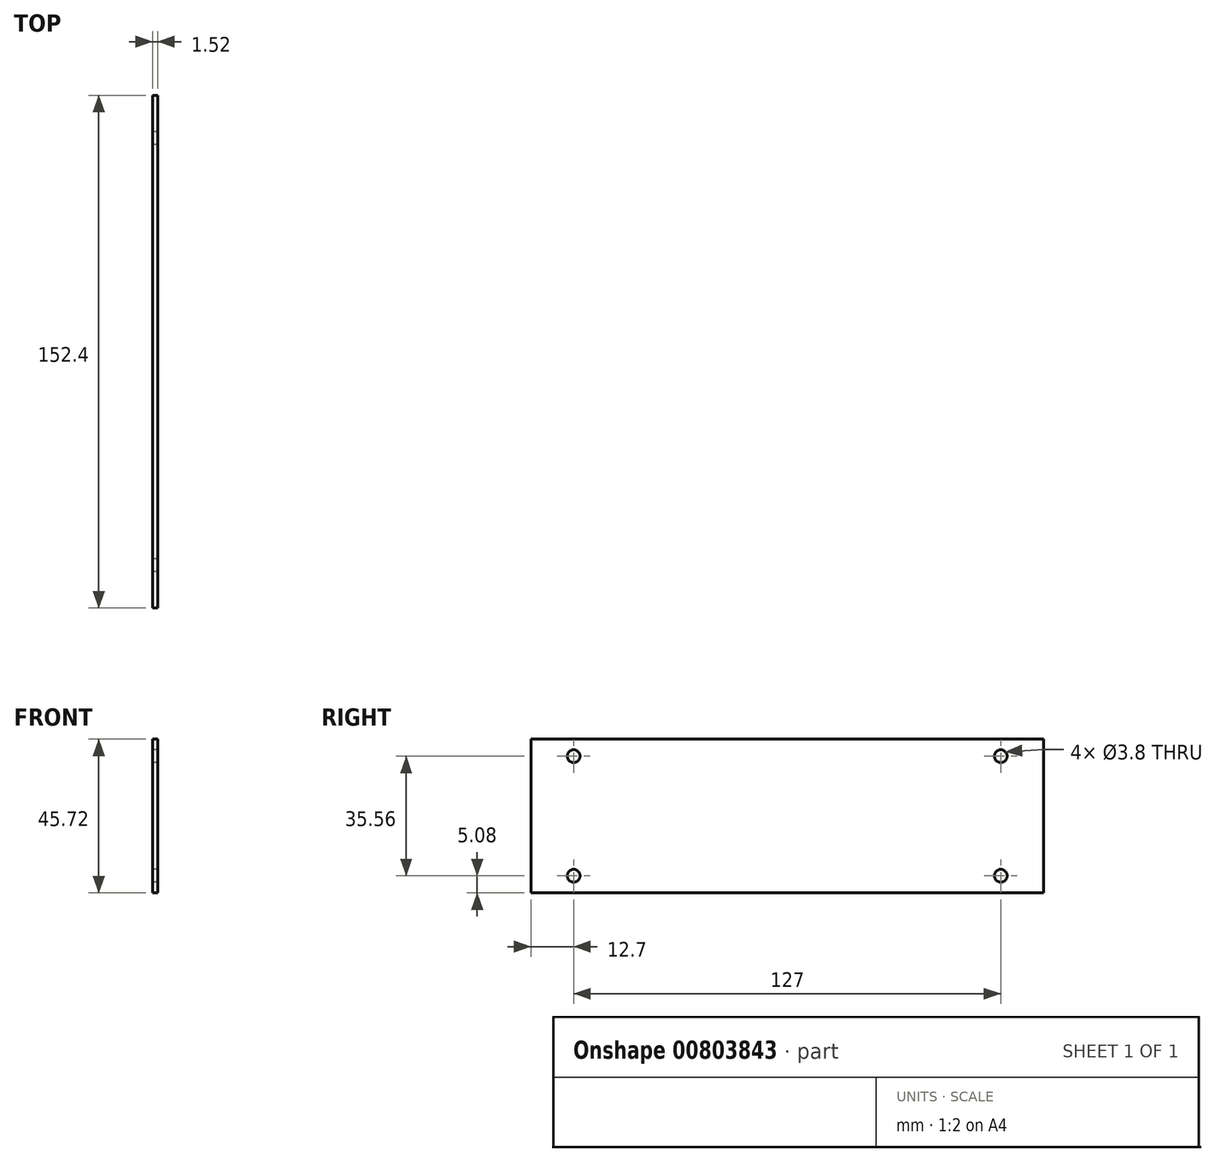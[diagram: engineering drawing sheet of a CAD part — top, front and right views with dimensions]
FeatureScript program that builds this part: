
annotation { "Feature Type Name" : "Feature", "Feature Type Description" : "" }
export const myFeature = defineFeature(function(context is Context, id is Id, definition is map)
    precondition{}
    {
        {
            var Q0;
            Q0=qCreatedBy(makeId("Right.planeOp"),FACE);
            var sketch = newSketch(context, id + "F0", { "sketchPlane" : qUnion([Q0])});
            skLineSegment(sketch, "E0.bottom", {"start": v(76.2, 22.86) * mm, "end": v(-76.2, 22.86) * mm});
            skLineSegment(sketch, "E0.top", {"start": v(76.2, -22.86) * mm, "end": v(-76.2, -22.86) * mm});
            skLineSegment(sketch, "E0.left", {"start": v(76.2, 22.86) * mm, "end": v(76.2, -22.86) * mm});
            skLineSegment(sketch, "E0.right", {"start": v(-76.2, 22.86) * mm, "end": v(-76.2, -22.86) * mm});
            skPoint(sketch, "E0.middle", {"position": v(0, 0) * mm});
            skLineSegment(sketch, "E1.bottom", {"start": v(63.5, 17.78) * mm, "end": v(-63.5, 17.78) * mm});
            skLineSegment(sketch, "E1.top", {"start": v(63.5, -17.78) * mm, "end": v(-63.5, -17.78) * mm});
            skLineSegment(sketch, "E1.left", {"start": v(63.5, 17.78) * mm, "end": v(63.5, -17.78) * mm});
            skLineSegment(sketch, "E1.right", {"start": v(-63.5, 17.78) * mm, "end": v(-63.5, -17.78) * mm});
            skSolve(sketch);
        }
        {
            var Q0;
            Q0=makeQuery(id+"F0.imprint","IMPRINT",FACE,{"disambiguationData":[TD([[makeQuery(id+"F0.imprint","IMPRINT",EDGE,{"derivedFrom":sQuery(id+"F0.wireOp",EDGE,"E0.bottom")}),1.0]])]});
            var Q1;
            Q1=makeQuery(id+"F0.imprint","IMPRINT",FACE,{"disambiguationData":[TD([[makeQuery(id+"F0.imprint","IMPRINT",EDGE,{"derivedFrom":sQuery(id+"F0.wireOp",EDGE,"E1.bottom")}),1.0]])]});
            extrude(context, id + "F1", {"entities" : qUnion([Q0, Q1]), "depth" : 1.52 * mm, "offsetDistance" : 25.4 * mm});
        }
        {
            var Q0;
            Q0=sQuery(id+"F0.wireOp",VERTEX,"E1.bottom.end");
            var Q1;
            Q1=sQuery(id+"F0.wireOp",VERTEX,"E1.bottom.start");
            var Q2;
            Q2=sQuery(id+"F0.wireOp",VERTEX,"E1.top.start");
            var Q3;
            Q3=sQuery(id+"F0.wireOp",VERTEX,"E1.top.end");
            var Q4;
            Q4=makeQuery(id+"F1.opExtrude","SWEPT_BODY",BODY,{"disambiguationData":[OSD([sQuery(id+"F0.wireOp",EDGE,"E0.bottom"),sQuery(id+"F0.wireOp",EDGE,"E0.top"),sQuery(id+"F0.wireOp",EDGE,"E0.left"),sQuery(id+"F0.wireOp",EDGE,"E0.right")])]});
            hole(context, id + "F2", {"style" : HoleStyle.SIMPLE, "endStyle" : HoleEndStyle.THROUGH, "oppositeDirection" : true, "standardTappedOrClearance" : lookupTablePath({ "standard" : "ANSI", "fit" : "Normal (ASME)", "size" : "#6", "type" : "Clearance" }), "standardBlindInLast" : lookupTablePath({ "fit" : "Free", "standard" : "ANSI", "size" : "#6", "type" : "Clearance" }), "holeDiameter" : 3.8 * mm, "majorDiameter" : 6.35 * mm, "isTappedThrough" : true, "tappedDepth" : 12.7 * mm, "tapClearance" : 3, "locations" : qUnion([Q0, Q1, Q2, Q3]), "scope" : qUnion([Q4])});
        }
    });
